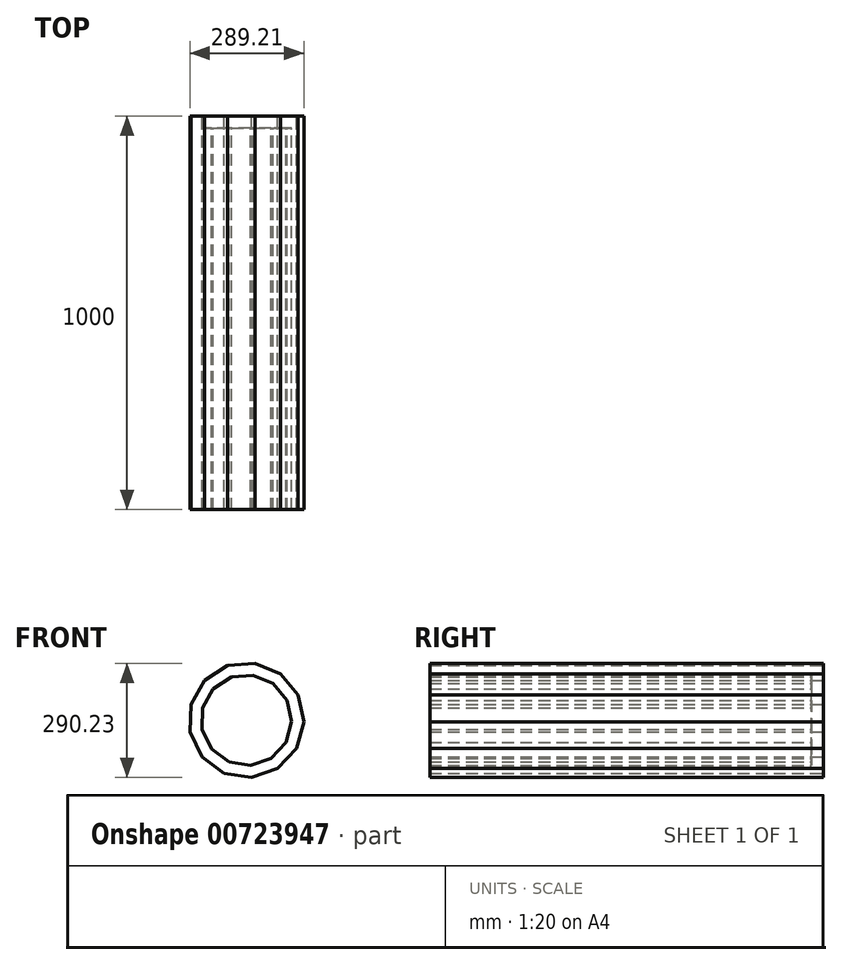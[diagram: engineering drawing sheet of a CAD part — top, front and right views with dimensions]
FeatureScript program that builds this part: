
annotation { "Feature Type Name" : "Feature", "Feature Type Description" : "" }
export const myFeature = defineFeature(function(context is Context, id is Id, definition is map)
    precondition{}
    {
        {
            var Q0;
            Q0=qCreatedBy(makeId("Front.planeOp"),FACE);
            var sketch = newSketch(context, id + "F0", { "sketchPlane" : qUnion([Q0])});
            skCircle(sketch, "E0.cCircle", {"center": v(0, 0) * mm, "radius": 142 * mm, "construction": true});
            skLineSegment(sketch, "E0.0", {"start": v(-140.83, 39.44) * mm, "end": v(-106.37, 100.37) * mm});
            skLineSegment(sketch, "E0.1", {"start": v(-106.37, 100.37) * mm, "end": v(-47.55, 138.3) * mm});
            skLineSegment(sketch, "E0.2", {"start": v(-47.55, 138.3) * mm, "end": v(22.17, 144.56) * mm});
            skLineSegment(sketch, "E0.3", {"start": v(22.17, 144.56) * mm, "end": v(86.81, 117.7) * mm});
            skLineSegment(sketch, "E0.4", {"start": v(86.81, 117.7) * mm, "end": v(131.57, 63.87) * mm});
            skLineSegment(sketch, "E0.5", {"start": v(131.57, 63.87) * mm, "end": v(146.18, -4.59) * mm});
            skLineSegment(sketch, "E0.6", {"start": v(146.18, -4.59) * mm, "end": v(127.3, -72) * mm});
            skLineSegment(sketch, "E0.7", {"start": v(127.3, -72) * mm, "end": v(79.26, -122.9) * mm});
            skLineSegment(sketch, "E0.8", {"start": v(79.26, -122.9) * mm, "end": v(13.07, -145.67) * mm});
            skLineSegment(sketch, "E0.9", {"start": v(13.07, -145.67) * mm, "end": v(-56.13, -135.05) * mm});
            skLineSegment(sketch, "E0.10", {"start": v(-56.13, -135.05) * mm, "end": v(-112.46, -93.5) * mm});
            skLineSegment(sketch, "E0.11", {"start": v(-112.46, -93.5) * mm, "end": v(-143.03, -30.53) * mm});
            skLineSegment(sketch, "E0.12", {"start": v(-143.03, -30.53) * mm, "end": v(-140.83, 39.44) * mm});
            skPoint(sketch, "E0.0.midPoint", {"position": v(-123.6, 69.9) * mm});
            skSolve(sketch);
        }
        {
            var Q0;
            Q0 = qSketchRegion(id + "F0", true);
            extrude(context, id + "F1", {"entities" : qUnion([Q0]), "depth" : 1000 * mm, "offsetDistance" : 25.4 * mm});
        }
        {
            var Q0;
            Q0=makeQuery(id+"F1.opExtrude","CAP_FACE",FACE,{"disambiguationData":[OSD([sQuery(id+"F0.wireOp",EDGE,"E0.0"),sQuery(id+"F0.wireOp",EDGE,"E0.1"),sQuery(id+"F0.wireOp",EDGE,"E0.2"),sQuery(id+"F0.wireOp",EDGE,"E0.3"),sQuery(id+"F0.wireOp",EDGE,"E0.4"),sQuery(id+"F0.wireOp",EDGE,"E0.5"),sQuery(id+"F0.wireOp",EDGE,"E0.6"),sQuery(id+"F0.wireOp",EDGE,"E0.7"),sQuery(id+"F0.wireOp",EDGE,"E0.8"),sQuery(id+"F0.wireOp",EDGE,"E0.9"),sQuery(id+"F0.wireOp",EDGE,"E0.10"),sQuery(id+"F0.wireOp",EDGE,"E0.11"),sQuery(id+"F0.wireOp",EDGE,"E0.12")])],"isStart":false});
            shell(context, id + "F2", {"entities" : qUnion([Q0]), "thickness" : 30 * mm});
        }
    });
